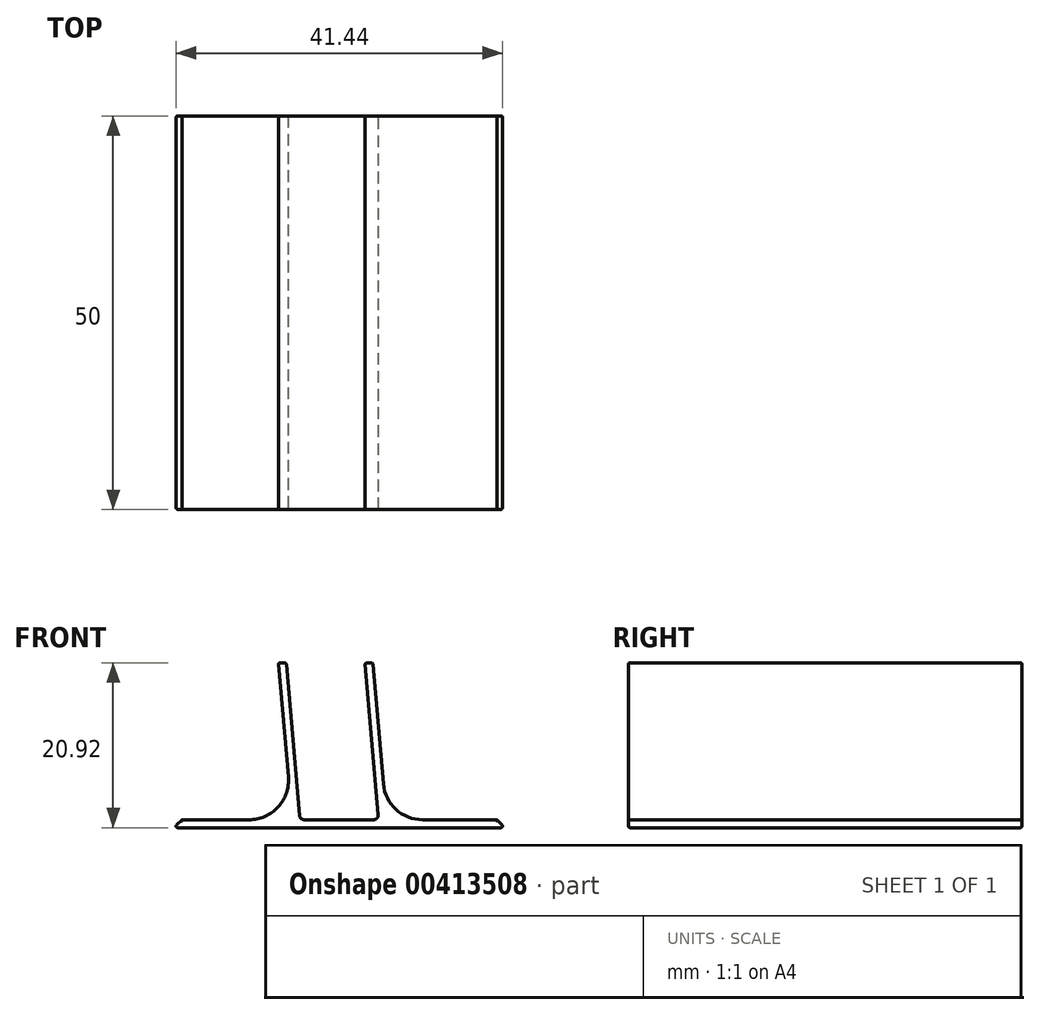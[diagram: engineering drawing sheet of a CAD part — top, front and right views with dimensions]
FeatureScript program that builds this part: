
annotation { "Feature Type Name" : "Feature", "Feature Type Description" : "" }
export const myFeature = defineFeature(function(context is Context, id is Id, definition is map)
    precondition{}
    {
        {
            var Q0;
            Q0=qCreatedBy(makeId("Front.planeOp"),FACE);
            var sketch = newSketch(context, id + "F0", { "sketchPlane" : qUnion([Q0])});
            skLineSegment(sketch, "E0", {"start": v(-5, 0) * mm, "end": v(5, 0) * mm});
            skLineSegment(sketch, "E1", {"start": v(5, 0) * mm, "end": v(3.26, 19.92) * mm});
            skLineSegment(sketch, "E2", {"start": v(0, 0) * mm, "end": v(0, -5.44) * mm, "construction": true});
            skLineSegment(sketch, "E3", {"start": v(-5, 0) * mm, "end": v(-6.74, 19.92) * mm});
            skLineSegment(sketch, "E4", {"start": v(-21, -1) * mm, "end": v(21, -1) * mm});
            skLineSegment(sketch, "E5", {"start": v(5, 0) * mm, "end": v(6, 0) * mm, "construction": true});
            skLineSegment(sketch, "E6", {"start": v(20, 0) * mm, "end": v(21, -1) * mm});
            skLineSegment(sketch, "E7", {"start": v(-5, 0) * mm, "end": v(-6, 0) * mm, "construction": true});
            skLineSegment(sketch, "E8", {"start": v(-21, -1) * mm, "end": v(-20, 0) * mm});
            skLineSegment(sketch, "E9", {"start": v(-6, 0) * mm, "end": v(-7.74, 19.92) * mm});
            skLineSegment(sketch, "E10", {"start": v(-7.74, 19.92) * mm, "end": v(-6.74, 19.92) * mm});
            skLineSegment(sketch, "E11", {"start": v(6, 0) * mm, "end": v(4.26, 19.92) * mm});
            skLineSegment(sketch, "E12", {"start": v(4.26, 19.92) * mm, "end": v(3.26, 19.92) * mm});
            skLineSegment(sketch, "E13", {"start": v(-6, 0) * mm, "end": v(-20, 0) * mm});
            skLineSegment(sketch, "E14", {"start": v(6, 0) * mm, "end": v(20, 0) * mm});
            skSolve(sketch);
        }
        {
            var Q0;
            Q0=makeQuery(id+"F0.imprint","IMPRINT",FACE,{"disambiguationData":[TD([[makeQuery(id+"F0.imprint","IMPRINT",EDGE,{"derivedFrom":sQuery(id+"F0.wireOp",EDGE,"E0")}),-1.0]])]});
            extrude(context, id + "F1", {"entities" : qUnion([Q0]), "depth" : 50 * mm});
        }
        {
            var Q0;
            Q0=makeQuery(id+"F1.opExtrude","SWEPT_EDGE",EDGE,{"disambiguationData":[OSD([sQuery(id+"F0.wireOp",EDGE,"E9"),sQuery(id+"F0.wireOp",EDGE,"E13")])]});
            var Q1;
            Q1=makeQuery(id+"F1.opExtrude","SWEPT_EDGE",EDGE,{"disambiguationData":[OSD([sQuery(id+"F0.wireOp",EDGE,"E11"),sQuery(id+"F0.wireOp",EDGE,"E14")])]});
            fillet(context, id + "F2", {"entities" : qUnion([Q0, Q1]), "radius" : 5 * mm, "tangentPropagation" : true, "allowEdgeOverflow" : false});
        }
        {
            var Q0;
            Q0=makeQuery(id+"F1.opExtrude","SWEPT_EDGE",EDGE,{"disambiguationData":[OSD([sQuery(id+"F0.wireOp",EDGE,"E0"),sQuery(id+"F0.wireOp",EDGE,"E3")])]});
            var Q1;
            Q1=makeQuery(id+"F1.opExtrude","SWEPT_EDGE",EDGE,{"disambiguationData":[OSD([sQuery(id+"F0.wireOp",EDGE,"E0"),sQuery(id+"F0.wireOp",EDGE,"E1")])]});
            fillet(context, id + "F3", {"entities" : qUnion([Q0, Q1]), "radius" : 0.6 * mm, "tangentPropagation" : true, "allowEdgeOverflow" : false});
        }
        {
            var Q0;
            Q0=makeQuery(id+"F1.opExtrude","SWEPT_FACE",FACE,{"disambiguationData":[OSD([sQuery(id+"F0.wireOp",EDGE,"E4")])]});
            var Q1;
            Q1=makeQuery(id+"F1.opExtrude","CAP_FACE",FACE,{"disambiguationData":[OSD([sQuery(id+"F0.wireOp",EDGE,"E0"),sQuery(id+"F0.wireOp",EDGE,"E1"),sQuery(id+"F0.wireOp",EDGE,"E3"),sQuery(id+"F0.wireOp",EDGE,"E4"),sQuery(id+"F0.wireOp",EDGE,"E6"),sQuery(id+"F0.wireOp",EDGE,"E8"),sQuery(id+"F0.wireOp",EDGE,"E9"),sQuery(id+"F0.wireOp",EDGE,"E10"),sQuery(id+"F0.wireOp",EDGE,"E11"),sQuery(id+"F0.wireOp",EDGE,"E12"),sQuery(id+"F0.wireOp",EDGE,"E13"),sQuery(id+"F0.wireOp",EDGE,"E14")])],"isStart":false});
            var Q2;
            Q2=makeQuery(id+"F1.opExtrude","CAP_FACE",FACE,{"disambiguationData":[OSD([sQuery(id+"F0.wireOp",EDGE,"E0"),sQuery(id+"F0.wireOp",EDGE,"E1"),sQuery(id+"F0.wireOp",EDGE,"E3"),sQuery(id+"F0.wireOp",EDGE,"E4"),sQuery(id+"F0.wireOp",EDGE,"E6"),sQuery(id+"F0.wireOp",EDGE,"E8"),sQuery(id+"F0.wireOp",EDGE,"E9"),sQuery(id+"F0.wireOp",EDGE,"E10"),sQuery(id+"F0.wireOp",EDGE,"E11"),sQuery(id+"F0.wireOp",EDGE,"E12"),sQuery(id+"F0.wireOp",EDGE,"E13"),sQuery(id+"F0.wireOp",EDGE,"E14")])],"isStart":true});
            fillet(context, id + "F4", {"entities" : qUnion([Q0, Q1, Q2]), "radius" : 0.2 * mm, "tangentPropagation" : true, "allowEdgeOverflow" : false});
        }
        {
            var Q0;
            Q0=makeQuery(id+"F1.opExtrude","SWEPT_FACE",FACE,{"disambiguationData":[OSD([sQuery(id+"F0.wireOp",EDGE,"E10")])]});
            var Q1;
            Q1=makeQuery(id+"F1.opExtrude","SWEPT_FACE",FACE,{"disambiguationData":[OSD([sQuery(id+"F0.wireOp",EDGE,"E12")])]});
            fillet(context, id + "F5", {"entities" : qUnion([Q0, Q1]), "radius" : 0.2 * mm, "tangentPropagation" : true, "allowEdgeOverflow" : false});
        }
    });
